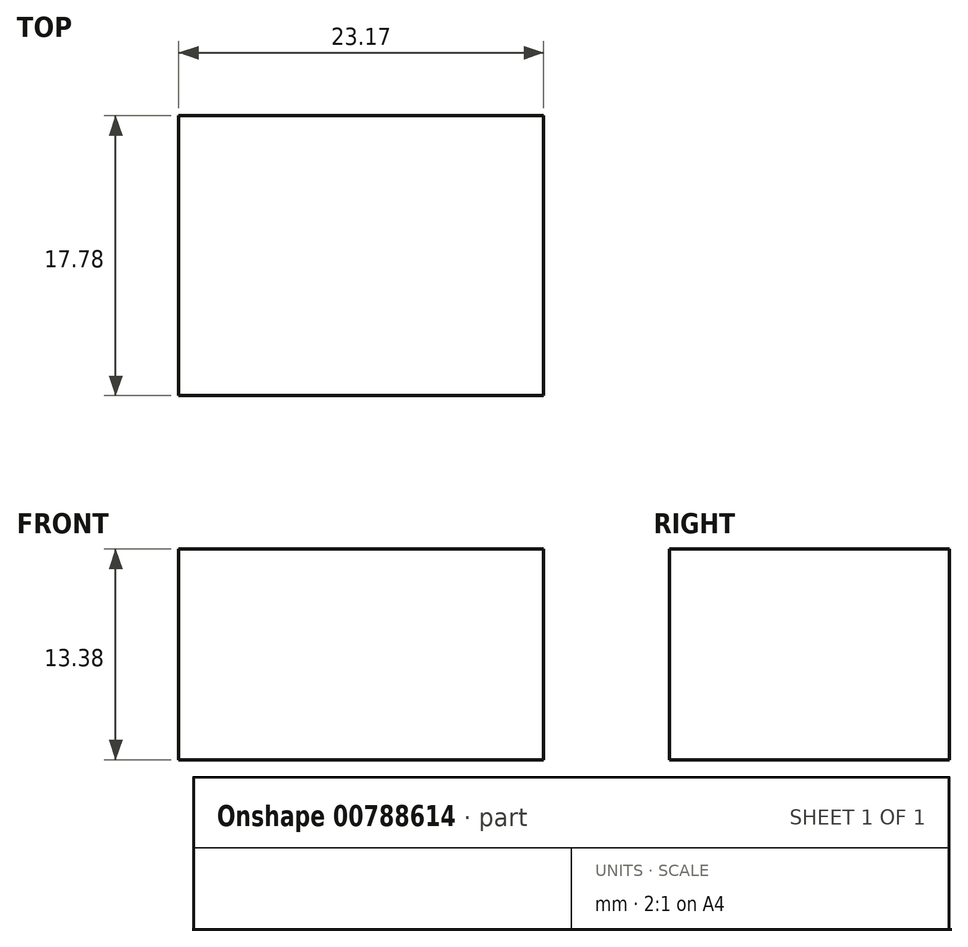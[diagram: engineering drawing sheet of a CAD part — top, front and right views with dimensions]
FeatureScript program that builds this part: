
annotation { "Feature Type Name" : "Feature", "Feature Type Description" : "" }
export const myFeature = defineFeature(function(context is Context, id is Id, definition is map)
    precondition{}
    {
        {
            var Q0;
            Q0=qCreatedBy(makeId("Front.planeOp"),FACE);
            var sketch = newSketch(context, id + "F0", { "sketchPlane" : qUnion([Q0])});
            skLineSegment(sketch, "E0.bottom", {"start": v(0, 0) * mm, "end": v(23.17, 0) * mm});
            skLineSegment(sketch, "E0.top", {"start": v(0, 13.38) * mm, "end": v(23.17, 13.38) * mm});
            skLineSegment(sketch, "E0.left", {"start": v(0, 0) * mm, "end": v(0, 13.38) * mm});
            skLineSegment(sketch, "E0.right", {"start": v(23.17, 0) * mm, "end": v(23.17, 13.38) * mm});
            skSolve(sketch);
        }
        {
            var Q0;
            Q0=makeQuery(id+"F0.imprint","IMPRINT",FACE,{"disambiguationData":[TD([[makeQuery(id+"F0.imprint","IMPRINT",EDGE,{"derivedFrom":sQuery(id+"F0.wireOp",EDGE,"E0.bottom")}),1.0]])]});
            extrude(context, id + "F1", {"entities" : qUnion([Q0]), "depth" : 17.78 * mm, "offsetDistance" : 25.4 * mm});
        }
    });
